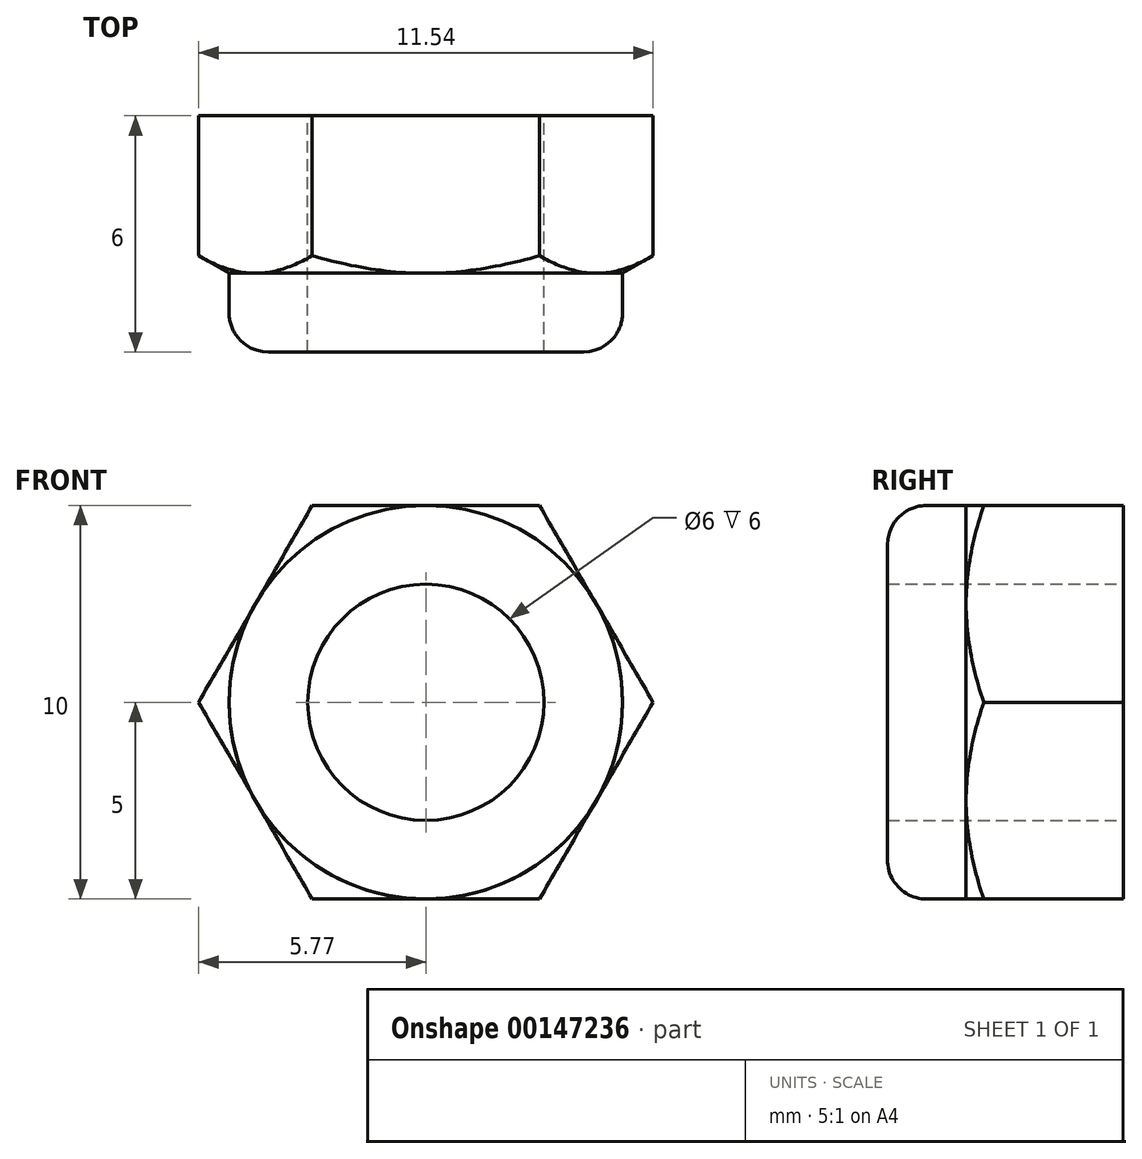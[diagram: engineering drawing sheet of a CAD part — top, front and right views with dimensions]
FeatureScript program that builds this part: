
annotation { "Feature Type Name" : "Feature", "Feature Type Description" : "" }
export const myFeature = defineFeature(function(context is Context, id is Id, definition is map)
    precondition{}
    {
        {
            var Q0;
            Q0=qCreatedBy(makeId("Front.planeOp"),FACE);
            var sketch = newSketch(context, id + "F0", { "sketchPlane" : qUnion([Q0])});
            skCircle(sketch, "E0.cCircle", {"center": v(0, 0) * mm, "radius": 5 * mm, "construction": true});
            skLineSegment(sketch, "E0.0", {"start": v(5.77, 0) * mm, "end": v(2.89, -5) * mm});
            skLineSegment(sketch, "E0.1", {"start": v(2.89, -5) * mm, "end": v(-2.89, -5) * mm});
            skLineSegment(sketch, "E0.2", {"start": v(-2.89, -5) * mm, "end": v(-5.77, 0) * mm});
            skLineSegment(sketch, "E0.3", {"start": v(-5.77, 0) * mm, "end": v(-2.89, 5) * mm});
            skLineSegment(sketch, "E0.4", {"start": v(-2.89, 5) * mm, "end": v(2.89, 5) * mm});
            skLineSegment(sketch, "E0.5", {"start": v(2.89, 5) * mm, "end": v(5.77, 0) * mm});
            skPoint(sketch, "E0.0.midPoint", {"position": v(4.33, -2.5) * mm});
            skCircle(sketch, "E1", {"center": v(0, 0) * mm, "radius": 3 * mm});
            skSolve(sketch);
        }
        {
            var Q0;
            Q0 = qSketchRegion(id + "F0", true);
            extrude(context, id + "F1", {"entities" : qUnion([Q0]), "depth" : 4 * mm});
        }
        {
            var Q0;
            Q0=qCreatedBy(makeId("Right.planeOp"),FACE);
            var sketch = newSketch(context, id + "F2", { "sketchPlane" : qUnion([Q0])});
            skLineSegment(sketch, "E2", {"start": v(-5.44, 2.5) * mm, "end": v(-2.56, 7.5) * mm});
            skLineSegment(sketch, "E3", {"start": v(-2.56, 7.5) * mm, "end": v(-5.44, 7.5) * mm});
            skLineSegment(sketch, "E4", {"start": v(-5.44, 7.5) * mm, "end": v(-5.44, 2.5) * mm});
            skLineSegment(sketch, "E5.0", {"start": v(-4, 5) * mm, "end": v(0, 5) * mm, "construction": true});
            skLineSegment(sketch, "E6", {"start": v(0, 0) * mm, "end": v(-18.75, 0) * mm, "construction": true});
            skSolve(sketch);
        }
        {
            var Q0;
            Q0 = qSketchRegion(id + "F2", true);
            var Q1;
            Q1=makeQuery(id+"F1.opExtrude","SWEPT_FACE",FACE,{"disambiguationData":[OSD([sQuery(id+"F0.wireOp",EDGE,"E1")])]});
            revolve(context, id + "F3", {"operationType" : NewBodyOperationType.REMOVE, "entities" : qUnion([Q0]), "axis" : qUnion([Q1]), "revolveType" : RevolveType.FULL});
        }
        {
            var Q0;
            Q0=makeQuery(id+"F1.opExtrude","CAP_FACE",FACE,{"disambiguationData":[OSD([sQuery(id+"F0.wireOp",EDGE,"E0.0"),sQuery(id+"F0.wireOp",EDGE,"E0.1"),sQuery(id+"F0.wireOp",EDGE,"E0.2"),sQuery(id+"F0.wireOp",EDGE,"E0.3"),sQuery(id+"F0.wireOp",EDGE,"E0.4"),sQuery(id+"F0.wireOp",EDGE,"E0.5"),sQuery(id+"F0.wireOp",EDGE,"E1")])],"isStart":false});
            var sketch = newSketch(context, id + "F4", { "sketchPlane" : qUnion([Q0])});
            skCircle(sketch, "E7", {"center": v(0, 0) * mm, "radius": 5 * mm});
            skCircle(sketch, "E8", {"center": v(0, 0) * mm, "radius": 3 * mm});
            skSolve(sketch);
        }
        {
            var Q0;
            Q0 = qSketchRegion(id + "F4", true);
            extrude(context, id + "F5", {"entities" : qUnion([Q0]), "operationType" : NewBodyOperationType.ADD, "depth" : 2 * mm});
        }
        {
            var Q0;
            Q0=makeQuery(id+"F5.opExtrude","CAP_EDGE",EDGE,{"disambiguationData":[OSD([sQuery(id+"F4.wireOp",EDGE,"E7")])],"isStart":false});
            fillet(context, id + "F6", {"entities" : qUnion([Q0]), "radius" : 1 * mm, "tangentPropagation" : true, "allowEdgeOverflow" : false});
        }
    });
